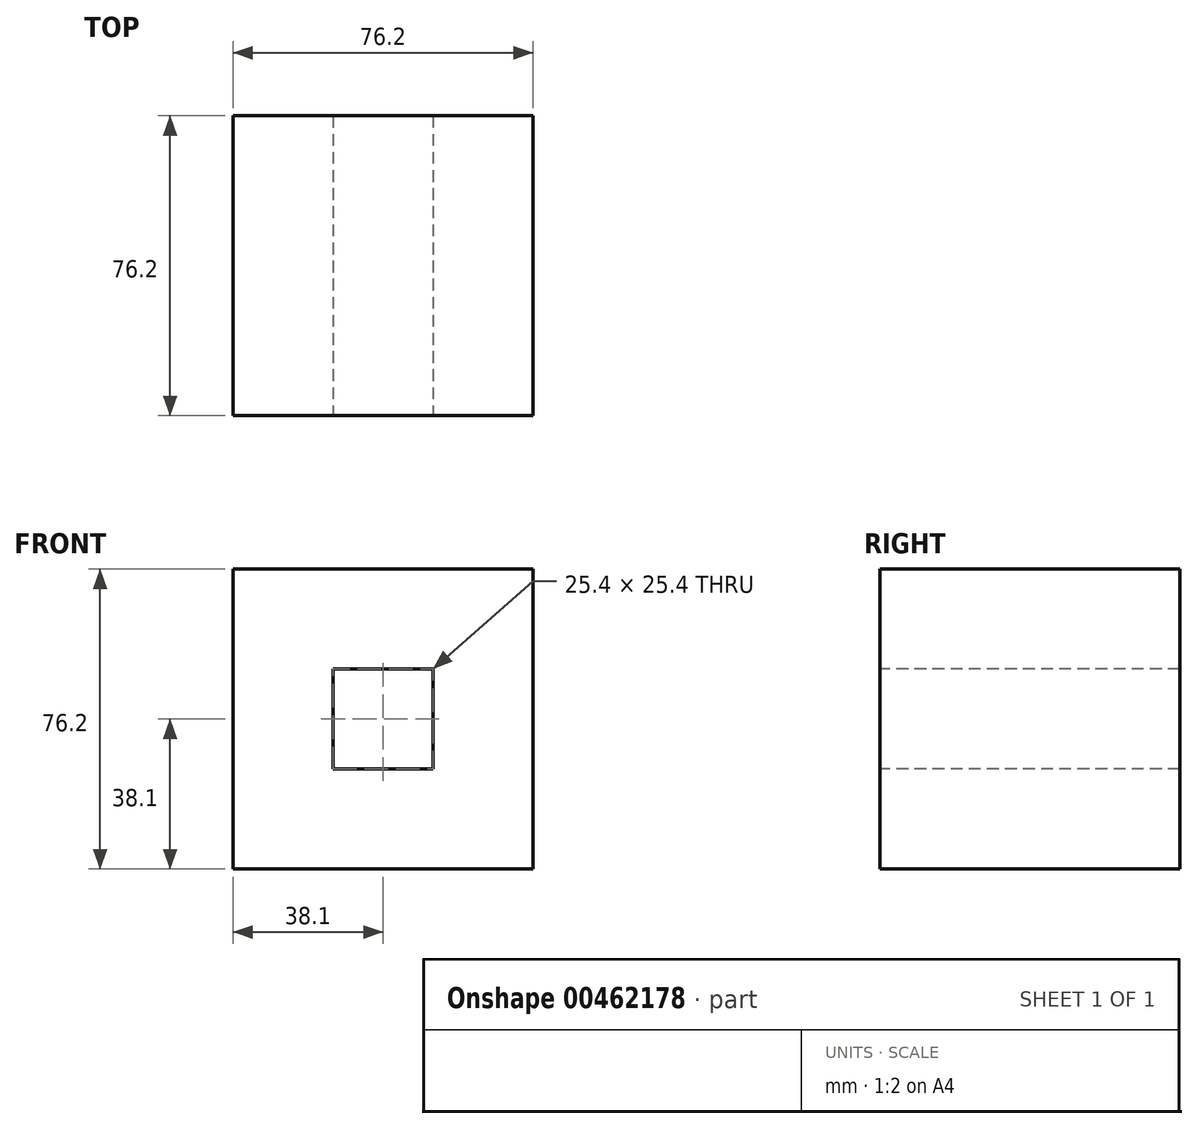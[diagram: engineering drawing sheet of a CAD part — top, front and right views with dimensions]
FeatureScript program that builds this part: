
annotation { "Feature Type Name" : "Feature", "Feature Type Description" : "" }
export const myFeature = defineFeature(function(context is Context, id is Id, definition is map)
    precondition{}
    {
        {
            var Q0;
            Q0=qCreatedBy(makeId("Front.planeOp"),FACE);
            var sketch = newSketch(context, id + "F0", { "sketchPlane" : qUnion([Q0])});
            skLineSegment(sketch, "E0.bottom", {"start": v(38.1, -38.1) * mm, "end": v(-38.1, -38.1) * mm});
            skLineSegment(sketch, "E0.top", {"start": v(38.1, 38.1) * mm, "end": v(-38.1, 38.1) * mm});
            skLineSegment(sketch, "E0.left", {"start": v(38.1, -38.1) * mm, "end": v(38.1, 38.1) * mm});
            skLineSegment(sketch, "E0.right", {"start": v(-38.1, -38.1) * mm, "end": v(-38.1, 38.1) * mm});
            skPoint(sketch, "E0.middle", {"position": v(0, 0) * mm});
            skSolve(sketch);
        }
        {
            var Q0;
            Q0 = qSketchRegion(id + "F0", true);
            extrude(context, id + "F1", {"entities" : qUnion([Q0]), "depth" : 76.2 * mm});
        }
        {
            var Q0;
            Q0=makeQuery(id+"F1.opExtrude","CAP_FACE",FACE,{"disambiguationData":[OSD([sQuery(id+"F0.wireOp",EDGE,"E0.bottom"),sQuery(id+"F0.wireOp",EDGE,"E0.top"),sQuery(id+"F0.wireOp",EDGE,"E0.left"),sQuery(id+"F0.wireOp",EDGE,"E0.right")])],"isStart":false});
            var sketch = newSketch(context, id + "F2", { "sketchPlane" : qUnion([Q0])});
            skLineSegment(sketch, "E1.bottom", {"start": v(12.7, -12.7) * mm, "end": v(-12.7, -12.7) * mm});
            skLineSegment(sketch, "E1.top", {"start": v(12.7, 12.7) * mm, "end": v(-12.7, 12.7) * mm});
            skLineSegment(sketch, "E1.left", {"start": v(12.7, -12.7) * mm, "end": v(12.7, 12.7) * mm});
            skLineSegment(sketch, "E1.right", {"start": v(-12.7, -12.7) * mm, "end": v(-12.7, 12.7) * mm});
            skPoint(sketch, "E1.middle", {"position": v(0, 0) * mm});
            skSolve(sketch);
        }
        {
            var Q0;
            Q0=makeQuery(id+"F2.imprint","IMPRINT",FACE,{"disambiguationData":[TD([[makeQuery(id+"F2.imprint","IMPRINT",EDGE,{"derivedFrom":sQuery(id+"F2.wireOp",EDGE,"E1.bottom")}),-1.0]])]});
            var Q1;
            Q1 = qSketchRegion(id + "F2", true);
            extrude(context, id + "F3", {"entities" : qUnion([Q0, Q1]), "operationType" : NewBodyOperationType.REMOVE, "endBound" : BoundingType.THROUGH_ALL, "oppositeDirection" : true, "depth" : 76.2 * mm});
        }
    });
